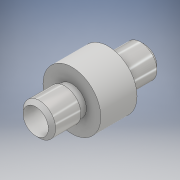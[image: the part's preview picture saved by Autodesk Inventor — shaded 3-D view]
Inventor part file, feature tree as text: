
AUTODESK INVENTOR PART (.ipt)
format: ipt  version: 2017 (Build 210142000, 142)  size: 144,896 bytes
history: native  units: mm
features: extrude x4, sketch x4, plane x2, chamfer x2
ambient origin geometry x8: Origin, YZ Plane, XZ Plane, XY Plane, X Axis, Y Axis, Z Axis, Center Point
bodies: Solid1 (feature_tree)
feature tree (12):
  extrude  "Extrusion1"  Depth=15.0mm TaperAngle=0.0deg
  extrude  "Extrusion2"  Depth=4.0mm TaperAngle=0.0deg
  extrude  "Extrusion3"  Depth=4.5mm
  plane  "Work Plane4"
  sketch  "Sketch4"  dims[d11=4.0mm d12=0.0mm d14=-4.0mm d15=11.5mm d16=4.0mm d17=8.0mm d26=0.5mm d27=2.0mm d28=45.0deg d29=0.5mm d30=2.0mm d31=45.0deg d32=5.0mm d33=0.0mm]
  chamfer  "Chamfer3"  [1 undecoded]
  chamfer  "Chamfer4"  Distance=11.5mm
  extrude  "Extrusion5"  Depth=4.0mm
  sketch  "Sketch1"  dims[d0=3.5mm d1=4.0mm d2=15.0mm d3=0.0mm]
  sketch  "Sketch2"  dims[d4=4.5mm d5=4.0mm d6=0.0mm d7=4.0mm d8=0.0mm]
  sketch  "Sketch3"  dims[d9=4.5mm d10=4.5mm]
  plane  "Work Plane3"
note: 1 required parameter value undecoded (feature->parameter linkage not recoverable at this tier; creation-order binding heuristic only, values carry confidence <= 0.55)
